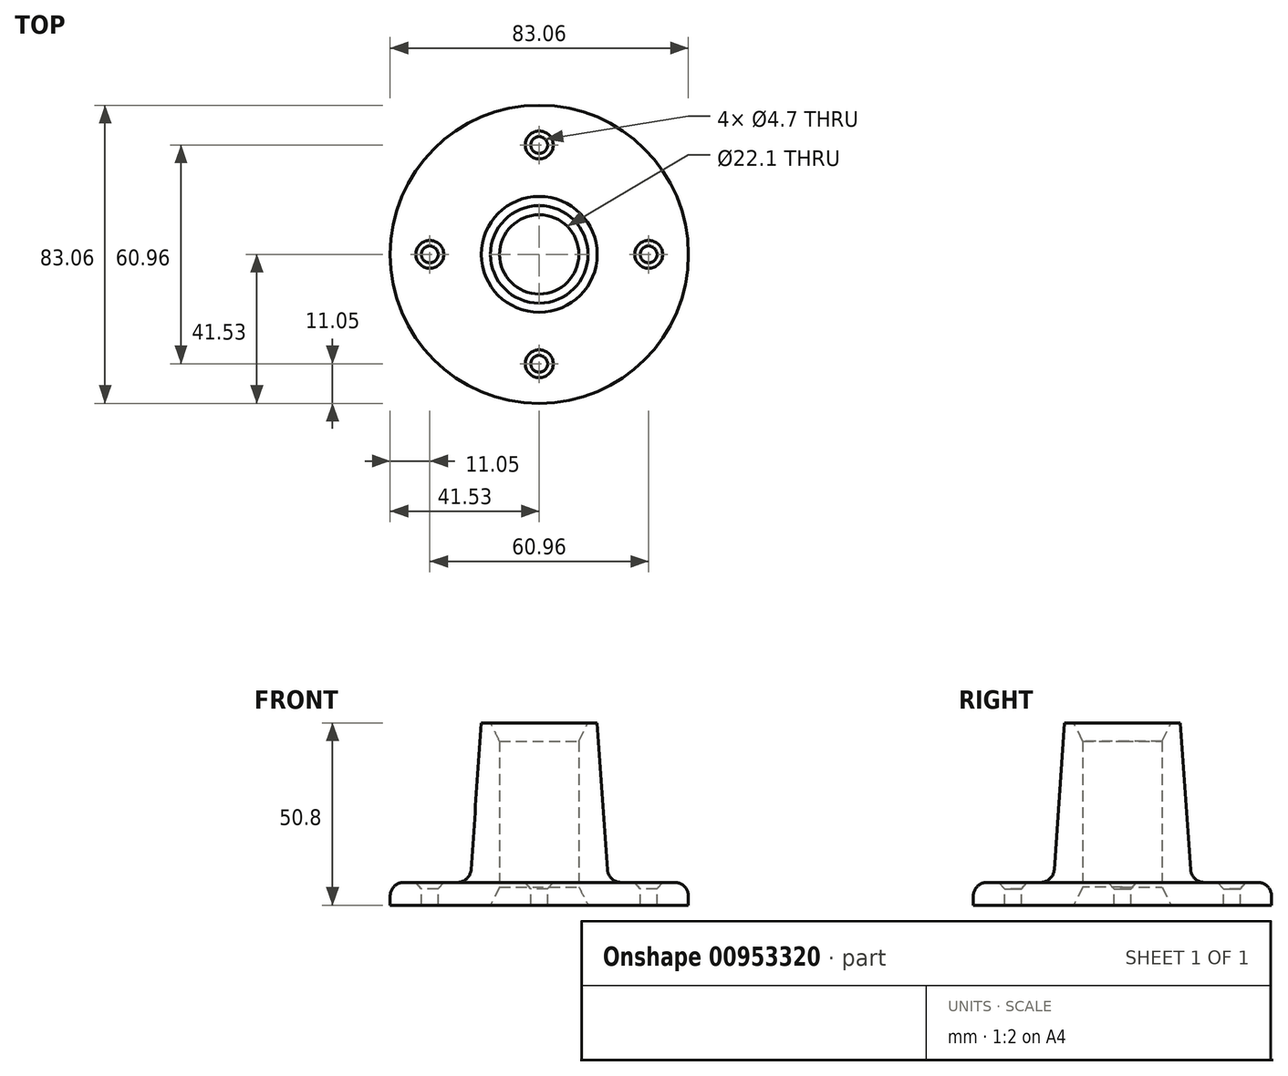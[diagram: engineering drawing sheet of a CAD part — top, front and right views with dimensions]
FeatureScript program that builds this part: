
annotation { "Feature Type Name" : "Feature", "Feature Type Description" : "" }
export const myFeature = defineFeature(function(context is Context, id is Id, definition is map)
    precondition{}
    {
        {
            var Q0;
            Q0=qCreatedBy(makeId("Front.planeOp"),FACE);
            var sketch = newSketch(context, id + "F0", { "sketchPlane" : qUnion([Q0])});
            skLineSegment(sketch, "E0", {"start": v(-11.05, 0) * mm, "end": v(-11.05, 50.8) * mm});
            skLineSegment(sketch, "E1", {"start": v(-11.05, 50.8) * mm, "end": v(-16.13, 50.8) * mm});
            skLineSegment(sketch, "E2", {"start": v(-16.13, 50.8) * mm, "end": v(-16.13, 6.35) * mm, "construction": true});
            skLineSegment(sketch, "E3", {"start": v(-19.24, 6.35) * mm, "end": v(-41.53, 6.35) * mm});
            skLineSegment(sketch, "E4", {"start": v(-41.53, 6.35) * mm, "end": v(-41.53, 0) * mm});
            skLineSegment(sketch, "E5", {"start": v(-41.53, 0) * mm, "end": v(-11.05, 0) * mm});
            skLineSegment(sketch, "E6", {"start": v(0, 0) * mm, "end": v(0, 11.33) * mm, "construction": true});
            skLineSegment(sketch, "E7", {"start": v(-16.13, 50.8) * mm, "end": v(-19.24, 6.35) * mm});
            skSolve(sketch);
        }
        {
            var Q0;
            Q0=makeQuery(id+"F0.imprint","IMPRINT",FACE,{"disambiguationData":[TD([[makeQuery(id+"F0.imprint","IMPRINT",EDGE,{"derivedFrom":sQuery(id+"F0.wireOp",EDGE,"E0")}),1.0]])]});
            var Q1;
            Q1=sQuery(id+"F0.wireOp",EDGE,"E6");
            revolve(context, id + "F1", {"surfaceOperationType" : NewSurfaceOperationType.NEW, "entities" : qUnion([Q0]), "axis" : qUnion([Q1]), "revolveType" : RevolveType.FULL});
        }
        {
            var Q0;
            Q0=makeQuery(id+"F1.opRevolve","SWEPT_FACE",FACE,{"disambiguationData":[OSD([sQuery(id+"F0.wireOp",EDGE,"E3")])]});
            var sketch = newSketch(context, id + "F2", { "sketchPlane" : qUnion([Q0])});
            skPoint(sketch, "E8", {"position": v(0, 30.48) * mm});
            skPoint(sketch, "E9", {"position": v(-30.48, 0) * mm});
            skPoint(sketch, "E10", {"position": v(0, -30.48) * mm});
            skPoint(sketch, "E11", {"position": v(30.48, 0) * mm});
            skCircle(sketch, "E12", {"center": v(0, 0) * mm, "radius": 30.48 * mm, "construction": true});
            skSolve(sketch);
        }
        {
            var Q0;
            Q0=sQuery(id+"F2.wireOp",VERTEX,"E9");
            var Q1;
            Q1=sQuery(id+"F2.wireOp",VERTEX,"E8");
            var Q2;
            Q2=sQuery(id+"F2.wireOp",VERTEX,"E11");
            var Q3;
            Q3=sQuery(id+"F2.wireOp",VERTEX,"E10");
            var Q4;
            Q4=makeQuery(id+"F1.opRevolve","SWEPT_BODY",BODY,{"disambiguationData":[OSD([sQuery(id+"F0.wireOp",EDGE,"E0"),sQuery(id+"F0.wireOp",EDGE,"E1"),sQuery(id+"F0.wireOp",EDGE,"E3"),sQuery(id+"F0.wireOp",EDGE,"E4"),sQuery(id+"F0.wireOp",EDGE,"E5"),sQuery(id+"F0.wireOp",EDGE,"E7")])]});
            hole(context, id + "F3", {"style" : HoleStyle.C_SINK, "endStyle" : HoleEndStyle.THROUGH, "standardTappedOrClearance" : lookupTablePath({ "fit" : "Loose (ASME)", "standard" : "ANSI", "size" : "#6", "type" : "Clearance" }), "standardBlindInLast" : lookupTablePath({ "fit" : "Loose", "standard" : "ANSI", "engagement" : "75%", "pitch" : "32 tpi", "size" : "#6", "type" : "Clearance & tapped" }), "holeDiameter" : 4.7 * mm, "cSinkDiameter" : 7.8 * mm, "cSinkAngle" : 82 * degree, "majorDiameter" : 6.35 * mm, "isTappedThrough" : true, "tappedDepth" : 12.7 * mm, "tapClearance" : 3, "locations" : qUnion([Q0, Q1, Q2, Q3]), "scope" : qUnion([Q4])});
        }
        {
            var Q0;
            Q0=makeQuery(id+"F1.opRevolve","SWEPT_EDGE",EDGE,{"disambiguationData":[OSD([sQuery(id+"F0.wireOp",EDGE,"E3"),sQuery(id+"F0.wireOp",EDGE,"E4")])]});
            var Q1;
            Q1=makeQuery(id+"F1.opRevolve","SWEPT_EDGE",EDGE,{"disambiguationData":[OSD([sQuery(id+"F0.wireOp",EDGE,"E3"),sQuery(id+"F0.wireOp",EDGE,"E7")])]});
            fillet(context, id + "F4", {"entities" : qUnion([Q0, Q1]), "radius" : 3.8 * mm, "tangentPropagation" : true, "allowEdgeOverflow" : false});
        }
        {
            var Q0;
            Q0=makeQuery(id+"F1.opRevolve","SWEPT_FACE",FACE,{"disambiguationData":[OSD([sQuery(id+"F0.wireOp",EDGE,"E0")])]});
            chamfer(context, id + "F5", {"entities" : qUnion([Q0]), "chamferType" : ChamferType.TWO_OFFSETS, "width1" : 2.54 * mm, "oppositeDirection" : true, "width2" : 5.08 * mm, "tangentPropagation" : true});
        }
    });
